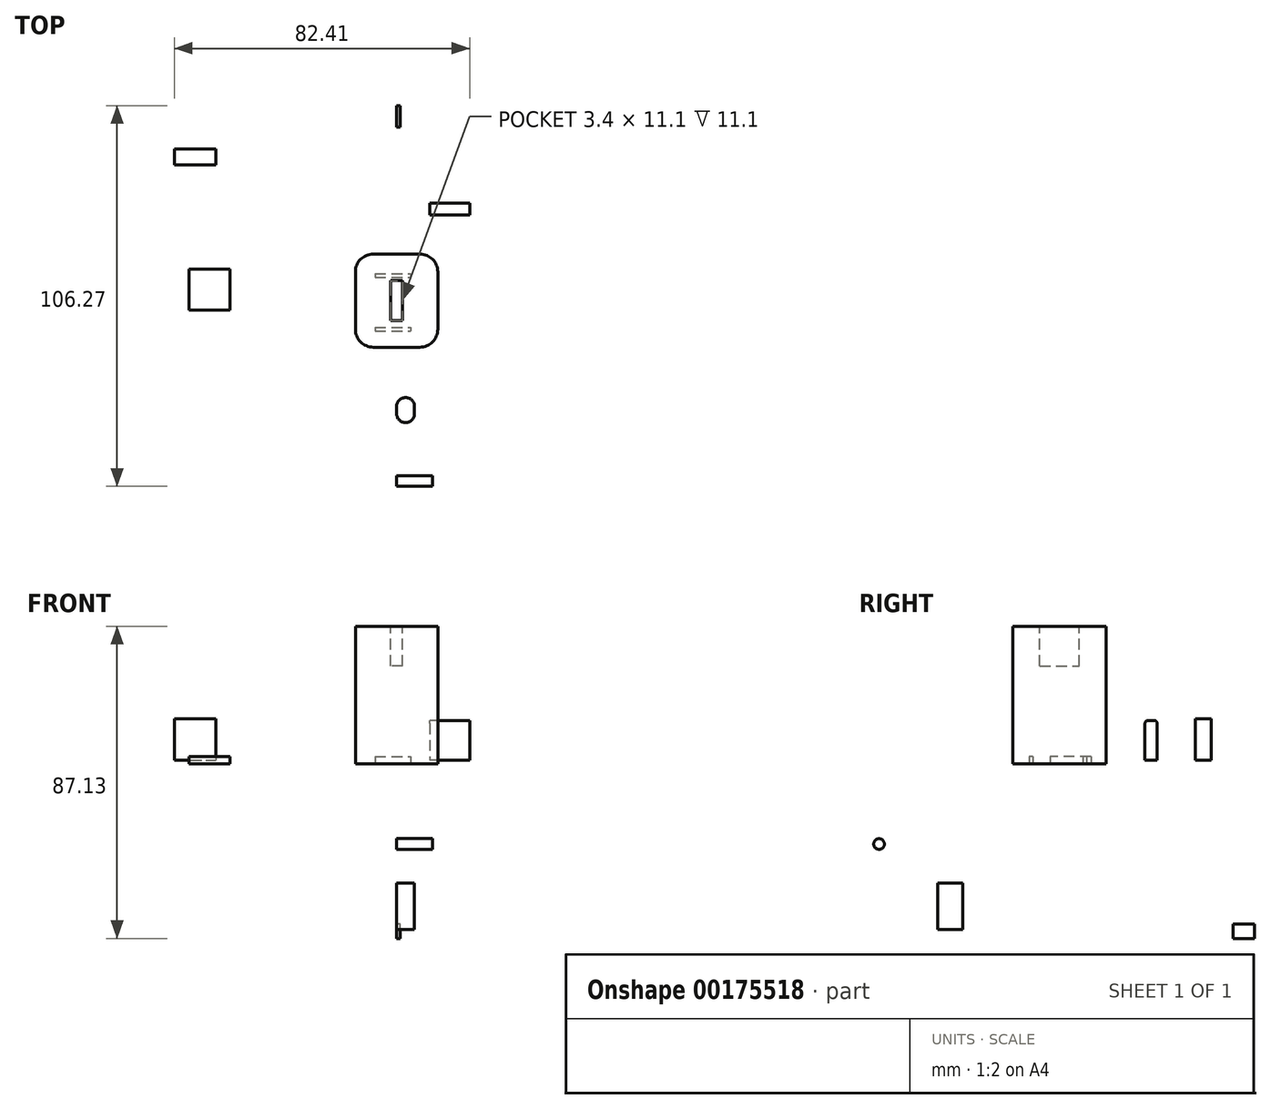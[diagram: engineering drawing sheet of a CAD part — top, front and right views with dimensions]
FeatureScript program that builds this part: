
annotation { "Feature Type Name" : "Feature", "Feature Type Description" : "" }
export const myFeature = defineFeature(function(context is Context, id is Id, definition is map)
    precondition{}
    {
        {
            var Q0;
            Q0=qCreatedBy(makeId("Top.planeOp"),FACE);
            var sketch = newSketch(context, id + "F0", { "sketchPlane" : qUnion([Q0])});
            skLineSegment(sketch, "E0.bottom", {"start": v(6.5, 13) * mm, "end": v(-6.5, 13) * mm});
            skLineSegment(sketch, "E0.top", {"start": v(6.5, -13) * mm, "end": v(-6.5, -13) * mm});
            skLineSegment(sketch, "E0.left", {"start": v(11.5, 8) * mm, "end": v(11.5, -8) * mm});
            skLineSegment(sketch, "E0.right", {"start": v(-11.5, 8) * mm, "end": v(-11.5, -8) * mm});
            skPoint(sketch, "E0.middle", {"position": v(0, 0) * mm});
            skPoint(sketch, "E1.visualSharp", {"position": v(-11.5, 13) * mm});
            skArc(sketch, "E1.filletArc", {"start": v(-6.5, 13) * mm, "mid": v(-10.04, 11.54) * mm, "end": v(-11.5, 8) * mm});
            skPoint(sketch, "E2.visualSharp", {"position": v(11.5, 13) * mm});
            skArc(sketch, "E2.filletArc", {"start": v(11.5, 8) * mm, "mid": v(10.04, 11.54) * mm, "end": v(6.5, 13) * mm});
            skPoint(sketch, "E3.visualSharp", {"position": v(11.5, -13) * mm});
            skArc(sketch, "E3.filletArc", {"start": v(6.5, -13) * mm, "mid": v(10.04, -11.54) * mm, "end": v(11.5, -8) * mm});
            skPoint(sketch, "E4.visualSharp", {"position": v(-11.5, -13) * mm});
            skArc(sketch, "E4.filletArc", {"start": v(-11.5, -8) * mm, "mid": v(-10.04, -11.54) * mm, "end": v(-6.5, -13) * mm});
            skLineSegment(sketch, "E5.bottom", {"start": v(-74.8, -30.07) * mm, "end": v(-38.76, -30.07) * mm});
            skLineSegment(sketch, "E5.top", {"start": v(-74.8, -65.15) * mm, "end": v(-38.76, -65.15) * mm});
            skLineSegment(sketch, "E5.left", {"start": v(-74.8, -30.07) * mm, "end": v(-74.8, -65.15) * mm});
            skPoint(sketch, "E6.end.orphan", {"position": v(-55.44, -42.51) * mm});
            skPoint(sketch, "E7.end.orphan", {"position": v(-38.94, -42.51) * mm});
            skPoint(sketch, "E8.center.orphan", {"position": v(-58.48, -47.51) * mm});
            skPoint(sketch, "E9.end.orphan", {"position": v(-63.04, -45.01) * mm});
            skPoint(sketch, "E10.end.orphan", {"position": v(-63.04, -50.01) * mm});
            skPoint(sketch, "E11.end.orphan", {"position": v(-38.94, -52.51) * mm});
            skPoint(sketch, "E11.start.orphan", {"position": v(-55.44, -52.51) * mm});
            skLineSegment(sketch, "E12.bottom", {"start": v(-57.85, 8.77) * mm, "end": v(-46.45, 8.77) * mm});
            skLineSegment(sketch, "E12.top", {"start": v(-57.85, -2.63) * mm, "end": v(-46.45, -2.63) * mm});
            skLineSegment(sketch, "E12.left", {"start": v(-57.85, 8.77) * mm, "end": v(-57.85, -2.63) * mm});
            skLineSegment(sketch, "E12.right", {"start": v(-46.45, 8.77) * mm, "end": v(-46.45, -2.63) * mm});
            skSolve(sketch);
        }
        {
            var Q0;
            Q0=makeQuery(id+"F0.imprint","IMPRINT",FACE,{"disambiguationData":[TD([[makeQuery(id+"F0.imprint","IMPRINT",EDGE,{"derivedFrom":sQuery(id+"F0.wireOp",EDGE,"E0.bottom")}),1.0]])]});
            extrude(context, id + "F1", {"entities" : qUnion([Q0]), "depth" : 37.4 * mm});
        }
        {
            var Q0;
            Q0=qSketchRegion(id+"F0",true);
            extrude(context, id + "F2", {"entities" : qUnion([Q0]), "operationType" : NewBodyOperationType.ADD, "depth" : 1 * mm, "hasSecondDirection" : true, "secondDirectionOppositeDirection" : true, "secondDirectionDepth" : 1 * mm});
        }
        {
            var Q0;
            Q0=qCreatedBy(makeId("Front.planeOp"),FACE);
            cPlane(context, id + "F3", {"entities" : qUnion([Q0]), "cplaneType" : CPlaneType.OFFSET, "offset" : 10 * mm, "width" : 150 * mm, "height" : 150 * mm});
        }
        {
            var Q0;
            Q0=qCreatedBy(makeId("Top.planeOp"),FACE);
            var sketch = newSketch(context, id + "F4", { "sketchPlane" : qUnion([Q0])});
            skLineSegment(sketch, "E13.bottom", {"start": v(20.4, 23.86) * mm, "end": v(9.3, 23.86) * mm});
            skLineSegment(sketch, "E13.top", {"start": v(20.4, 27.26) * mm, "end": v(9.3, 27.26) * mm});
            skLineSegment(sketch, "E13.left", {"start": v(20.4, 23.86) * mm, "end": v(20.4, 27.26) * mm});
            skLineSegment(sketch, "E13.right", {"start": v(9.3, 23.86) * mm, "end": v(9.3, 27.26) * mm});
            skPoint(sketch, "E13.middle", {"position": v(14.86, 25.56) * mm});
            skSolve(sketch);
        }
        {
            var Q0;
            Q0=makeQuery(id+"F4.imprint","IMPRINT",FACE,{"disambiguationData":[TD([[makeQuery(id+"F4.imprint","IMPRINT",EDGE,{"derivedFrom":sQuery(id+"F4.wireOp",EDGE,"E13.bottom")}),-1.0]])]});
            extrude(context, id + "F5", {"entities" : qUnion([Q0]), "depth" : 11.1 * mm});
        }
        {
            var Q0;
            Q0=qCreatedBy(makeId("Top.planeOp"),FACE);
            var sketch = newSketch(context, id + "F6", { "sketchPlane" : qUnion([Q0])});
            skLineSegment(sketch, "E14.bottom", {"start": v(-62, 42.3) * mm, "end": v(-50.4, 42.3) * mm});
            skLineSegment(sketch, "E14.top", {"start": v(-62, 37.9) * mm, "end": v(-50.4, 37.9) * mm});
            skLineSegment(sketch, "E14.left", {"start": v(-62, 42.3) * mm, "end": v(-62, 37.9) * mm});
            skLineSegment(sketch, "E14.right", {"start": v(-50.4, 42.3) * mm, "end": v(-50.4, 37.9) * mm});
            skSolve(sketch);
        }
        {
            var Q0;
            Q0=qSketchRegion(id+"F6",true);
            extrude(context, id + "F7", {"entities" : qUnion([Q0]), "depth" : 11.6 * mm});
        }
        {
            var Q0;
            Q0=qCreatedBy(makeId("Right.planeOp"),FACE);
            var sketch = newSketch(context, id + "F8", { "sketchPlane" : qUnion([Q0])});
            skCircle(sketch, "E15", {"center": v(-50.35, -23.39) * mm, "radius": 1.5 * mm});
            skSolve(sketch);
        }
        {
            var Q0;
            Q0=qSketchRegion(id+"F8",true);
            extrude(context, id + "F9", {"entities" : qUnion([Q0]), "depth" : 10 * mm});
        }
        {
            var Q0;
            Q0=qCreatedBy(makeId("Right.planeOp"),FACE);
            var sketch = newSketch(context, id + "F10", { "sketchPlane" : qUnion([Q0])});
            skLineSegment(sketch, "E16.bottom", {"start": v(54.42, -49.73) * mm, "end": v(48.42, -49.73) * mm});
            skLineSegment(sketch, "E16.top", {"start": v(54.42, -45.73) * mm, "end": v(48.42, -45.73) * mm});
            skLineSegment(sketch, "E16.left", {"start": v(54.42, -49.73) * mm, "end": v(54.42, -45.73) * mm});
            skLineSegment(sketch, "E16.right", {"start": v(48.42, -49.73) * mm, "end": v(48.42, -45.73) * mm});
            skPoint(sketch, "E16.middle", {"position": v(51.42, -47.73) * mm});
            skSolve(sketch);
        }
        {
            var Q0;
            Q0=makeQuery(id+"F10.imprint","IMPRINT",FACE,{"disambiguationData":[TD([[makeQuery(id+"F10.imprint","IMPRINT",EDGE,{"derivedFrom":sQuery(id+"F10.wireOp",EDGE,"E16.bottom")}),-1.0]])]});
            extrude(context, id + "F11", {"entities" : qUnion([Q0]), "depth" : 1 * mm});
        }
        {
            var Q0;
            Q0=qCreatedBy(makeId("Right.planeOp"),FACE);
            var sketch = newSketch(context, id + "F12", { "sketchPlane" : qUnion([Q0])});
            skLineSegment(sketch, "E17.bottom", {"start": v(-34.05, -34.27) * mm, "end": v(-27.05, -34.27) * mm});
            skLineSegment(sketch, "E17.top", {"start": v(-34.05, -47.27) * mm, "end": v(-27.05, -47.27) * mm});
            skLineSegment(sketch, "E17.left", {"start": v(-34.05, -34.27) * mm, "end": v(-34.05, -47.27) * mm});
            skLineSegment(sketch, "E17.right", {"start": v(-27.05, -34.27) * mm, "end": v(-27.05, -47.27) * mm});
            skSolve(sketch);
        }
        {
            var Q0;
            Q0=makeQuery(id+"F12.imprint","IMPRINT",FACE,{"disambiguationData":[TD([[makeQuery(id+"F12.imprint","IMPRINT",EDGE,{"derivedFrom":sQuery(id+"F12.wireOp",EDGE,"E17.bottom")}),-1.0]])]});
            extrude(context, id + "F13", {"entities" : qUnion([Q0]), "depth" : 5 * mm});
        }
        {
            var Q0;
            Q0=makeQuery(id+"F13.opExtrude","CAP_EDGE",EDGE,{"disambiguationData":[OSD([sQuery(id+"F12.wireOp",EDGE,"E17.left")])],"isStart":false});
            var Q1;
            Q1=makeQuery(id+"F13.opExtrude","CAP_EDGE",EDGE,{"disambiguationData":[OSD([sQuery(id+"F12.wireOp",EDGE,"E17.right")])],"isStart":false});
            var Q2;
            Q2=makeQuery(id+"F13.opExtrude","CAP_EDGE",EDGE,{"disambiguationData":[OSD([sQuery(id+"F12.wireOp",EDGE,"E17.right")])],"isStart":true});
            var Q3;
            Q3=makeQuery(id+"F13.opExtrude","CAP_EDGE",EDGE,{"disambiguationData":[OSD([sQuery(id+"F12.wireOp",EDGE,"E17.left")])],"isStart":true});
            fillet(context, id + "F14", {"entities" : qUnion([Q0, Q1, Q2, Q3]), "radius" : 2.5 * mm, "tangentPropagation" : true, "allowEdgeOverflow" : false});
        }
        {
            var Q0;
            Q0=makeQuery(id+"F1.opExtrude","CAP_FACE",FACE,{"disambiguationData":[OSD([sQuery(id+"F0.wireOp",EDGE,"E0.bottom"),sQuery(id+"F0.wireOp",EDGE,"E0.top"),sQuery(id+"F0.wireOp",EDGE,"E0.left"),sQuery(id+"F0.wireOp",EDGE,"E0.right"),sQuery(id+"F0.wireOp",EDGE,"E1.filletArc"),sQuery(id+"F0.wireOp",EDGE,"E2.filletArc"),sQuery(id+"F0.wireOp",EDGE,"E3.filletArc"),sQuery(id+"F0.wireOp",EDGE,"E4.filletArc")])],"isStart":false});
            var sketch = newSketch(context, id + "F15", { "sketchPlane" : qUnion([Q0])});
            skLineSegment(sketch, "E18.bottom", {"start": v(1.7, -5.55) * mm, "end": v(-1.7, -5.55) * mm});
            skLineSegment(sketch, "E18.top", {"start": v(1.7, 5.55) * mm, "end": v(-1.7, 5.55) * mm});
            skLineSegment(sketch, "E18.left", {"start": v(1.7, -5.55) * mm, "end": v(1.7, 5.55) * mm});
            skLineSegment(sketch, "E18.right", {"start": v(-1.7, -5.55) * mm, "end": v(-1.7, 5.55) * mm});
            skPoint(sketch, "E18.middle", {"position": v(0, 0) * mm});
            skSolve(sketch);
        }
        {
            var Q0;
            Q0=qSketchRegion(id+"F15",true);
            extrude(context, id + "F16", {"entities" : qUnion([Q0]), "operationType" : NewBodyOperationType.REMOVE, "oppositeDirection" : true, "depth" : 11.1 * mm});
        }
        {
            var Q0;
            Q0=makeQuery(id+"F5.opExtrude","CAP_EDGE",EDGE,{"disambiguationData":[OSD([sQuery(id+"F4.wireOp",EDGE,"E13.top")])],"isStart":false});
            var Q1;
            Q1=makeQuery(id+"F5.opExtrude","CAP_EDGE",EDGE,{"disambiguationData":[OSD([sQuery(id+"F4.wireOp",EDGE,"E13.bottom")])],"isStart":false});
            fillet(context, id + "F17", {"entities" : qUnion([Q0, Q1]), "radius" : 0.85 * mm, "allowEdgeOverflow" : false});
        }
        {
            var Q0;
            Q0=makeQuery(id+"F2.opExtrude","CAP_FACE",FACE,{"disambiguationData":[OSD([sQuery(id+"F0.wireOp",EDGE,"E0.bottom"),sQuery(id+"F0.wireOp",EDGE,"E0.top"),sQuery(id+"F0.wireOp",EDGE,"E0.left"),sQuery(id+"F0.wireOp",EDGE,"E0.right"),sQuery(id+"F0.wireOp",EDGE,"E1.filletArc"),sQuery(id+"F0.wireOp",EDGE,"E2.filletArc"),sQuery(id+"F0.wireOp",EDGE,"E3.filletArc"),sQuery(id+"F0.wireOp",EDGE,"E4.filletArc")])],"isStart":true});
            var sketch = newSketch(context, id + "F18", { "sketchPlane" : qUnion([Q0])});
            skLineSegment(sketch, "E19.bottom", {"start": v(-6, -7.5) * mm, "end": v(4, -7.5) * mm});
            skLineSegment(sketch, "E19.top", {"start": v(-6, -6.5) * mm, "end": v(4, -6.5) * mm});
            skLineSegment(sketch, "E19.left", {"start": v(-6, -7.5) * mm, "end": v(-6, -6.5) * mm});
            skLineSegment(sketch, "E19.right", {"start": v(4, -7.5) * mm, "end": v(4, -6.5) * mm});
            skLineSegment(sketch, "E20.bottom", {"start": v(-6, 7.5) * mm, "end": v(4, 7.5) * mm});
            skLineSegment(sketch, "E20.top", {"start": v(-6, 8.5) * mm, "end": v(4, 8.5) * mm});
            skLineSegment(sketch, "E20.left", {"start": v(-6, 7.5) * mm, "end": v(-6, 8.5) * mm});
            skLineSegment(sketch, "E20.right", {"start": v(4, 7.5) * mm, "end": v(4, 8.5) * mm});
            skSolve(sketch);
        }
        {
            var Q0;
            Q0=qSketchRegion(id+"F18",true);
            extrude(context, id + "F19", {"entities" : qUnion([Q0]), "operationType" : NewBodyOperationType.REMOVE, "oppositeDirection" : true, "depth" : 2 * mm});
        }
    });
